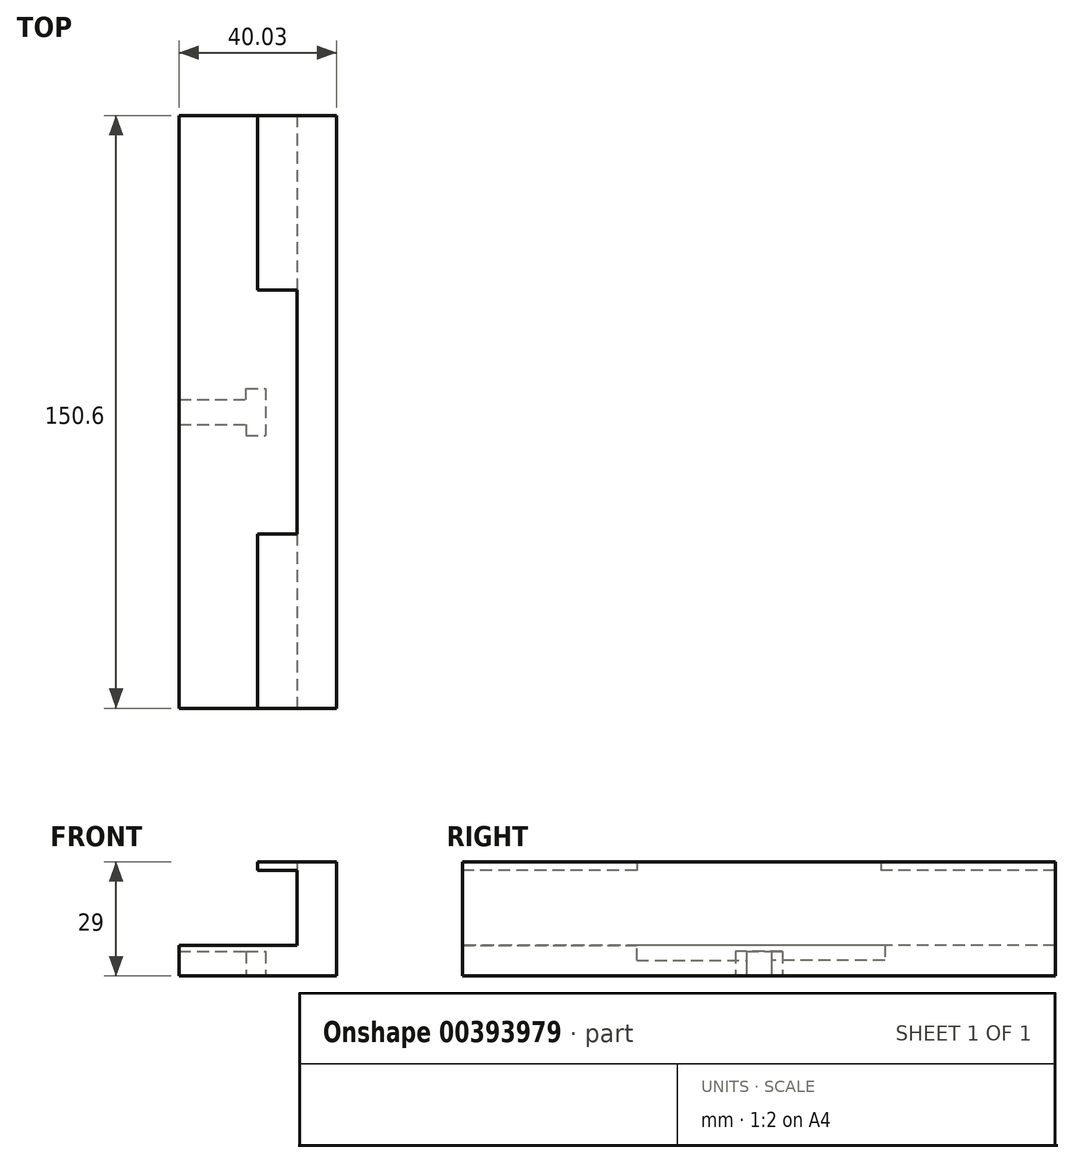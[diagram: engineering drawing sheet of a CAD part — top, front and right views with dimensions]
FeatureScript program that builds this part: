
annotation { "Feature Type Name" : "Feature", "Feature Type Description" : "" }
export const myFeature = defineFeature(function(context is Context, id is Id, definition is map)
    precondition{}
    {
        {
            var Q0;
            Q0=qCreatedBy(makeId("Top.planeOp"),FACE);
            var sketch = newSketch(context, id + "F0", { "sketchPlane" : qUnion([Q0])});
            skLineSegment(sketch, "E0", {"start": v(40.03, 80.64) * mm, "end": v(40.03, -69.96) * mm});
            skLineSegment(sketch, "E1", {"start": v(40.03, 80.64) * mm, "end": v(20.03, 80.64) * mm});
            skLineSegment(sketch, "E2", {"start": v(40.03, -69.96) * mm, "end": v(20.03, -69.96) * mm});
            skLineSegment(sketch, "E3", {"start": v(10.03, -69.96) * mm, "end": v(10.03, -25.66) * mm});
            skLineSegment(sketch, "E4", {"start": v(10.03, 80.64) * mm, "end": v(10.03, 36.34) * mm});
            skLineSegment(sketch, "E5", {"start": v(10.03, -25.66) * mm, "end": v(30.03, -25.66) * mm});
            skLineSegment(sketch, "E6", {"start": v(10.03, 36.34) * mm, "end": v(30.03, 36.34) * mm});
            skLineSegment(sketch, "E7", {"start": v(30.03, -25.66) * mm, "end": v(30.03, 36.34) * mm});
            skLineSegment(sketch, "E8", {"start": v(10.03, 80.64) * mm, "end": v(20.03, 80.64) * mm});
            skLineSegment(sketch, "E9", {"start": v(10.03, -69.96) * mm, "end": v(20.03, -69.96) * mm});
            skSolve(sketch);
        }
        {
            var Q0;
            Q0 = qSketchRegion(id + "F0", true);
            extrude(context, id + "F1", {"entities" : qUnion([Q0]), "depth" : 25 * mm});
        }
        {
            var Q0;
            Q0=makeQuery(id+"F16.boolean.opBoolean","MERGE",FACE,{"derivedFrom":[makeQuery(id+"F14.boolean.opBoolean","MERGE",FACE,{"derivedFrom":[makeQuery(id+"F12.boolean.opBoolean","MERGE",FACE,{"derivedFrom":[makeQuery(id+"F1.opExtrude","CAP_FACE",FACE,{"disambiguationData":[OSD([sQuery(id+"F0.wireOp",EDGE,"E0"),sQuery(id+"F0.wireOp",EDGE,"E1"),sQuery(id+"F0.wireOp",EDGE,"E2"),sQuery(id+"F0.wireOp",EDGE,"E3"),sQuery(id+"F0.wireOp",EDGE,"E4"),sQuery(id+"F0.wireOp",EDGE,"E5"),sQuery(id+"F0.wireOp",EDGE,"E6"),sQuery(id+"F0.wireOp",EDGE,"E7"),sQuery(id+"F0.wireOp",EDGE,"E8"),sQuery(id+"F0.wireOp",EDGE,"E9")])],"isStart":true}),makeQuery(id+"F12.opExtrude","SWEPT_FACE",FACE,{"disambiguationData":[OSD([sQuery(id+"F11.wireOp",EDGE,"E30")])]})]}),makeQuery(id+"F14.opExtrude","SWEPT_FACE",FACE,{"disambiguationData":[OSD([sQuery(id+"F13.wireOp",EDGE,"E34")])]})]}),makeQuery(id+"F16.opExtrude","SWEPT_FACE",FACE,{"disambiguationData":[OSD([sQuery(id+"F15.wireOp",EDGE,"E36")])]})]});
            var sketch = newSketch(context, id + "F2", { "sketchPlane" : qUnion([Q0])});
            skLineSegment(sketch, "E10.bottom", {"start": v(0.03, 69.96) * mm, "end": v(40.03, 69.96) * mm});
            skLineSegment(sketch, "E10.top", {"start": v(0.03, -80.64) * mm, "end": v(40.03, -80.64) * mm});
            skLineSegment(sketch, "E10.left", {"start": v(0.03, 69.96) * mm, "end": v(0.03, -80.64) * mm});
            skLineSegment(sketch, "E10.right", {"start": v(40.03, 69.96) * mm, "end": v(40.03, -80.64) * mm});
            skSolve(sketch);
        }
        {
            var Q0;
            Q0=makeQuery(id+"F1.opExtrude","SWEPT_FACE",FACE,{"disambiguationData":[OSD([sQuery(id+"F0.wireOp",EDGE,"E4")])]});
            var sketch = newSketch(context, id + "F3", { "sketchPlane" : qUnion([Q0])});
            skLineSegment(sketch, "E11", {"start": v(-80.64, 22.8) * mm, "end": v(-36.34, 22.8) * mm});
            skLineSegment(sketch, "E12", {"start": v(-80.64, 22.8) * mm, "end": v(-80.64, 3.8) * mm});
            skLineSegment(sketch, "E13", {"start": v(-80.64, 3.8) * mm, "end": v(-36.34, 3.8) * mm});
            skLineSegment(sketch, "E14", {"start": v(-36.34, 3.8) * mm, "end": v(-36.34, 22.8) * mm});
            skSolve(sketch);
        }
        {
            var Q0;
            Q0 = qSketchRegion(id + "F3", true);
            extrude(context, id + "F4", {"entities" : qUnion([Q0]), "operationType" : NewBodyOperationType.REMOVE, "oppositeDirection" : true, "depth" : 20 * mm});
        }
        {
            var Q0;
            Q0=makeQuery(id+"F1.opExtrude","CAP_FACE",FACE,{"disambiguationData":[OSD([sQuery(id+"F0.wireOp",EDGE,"E0"),sQuery(id+"F0.wireOp",EDGE,"E1"),sQuery(id+"F0.wireOp",EDGE,"E2"),sQuery(id+"F0.wireOp",EDGE,"E3"),sQuery(id+"F0.wireOp",EDGE,"E4"),sQuery(id+"F0.wireOp",EDGE,"E5"),sQuery(id+"F0.wireOp",EDGE,"E6"),sQuery(id+"F0.wireOp",EDGE,"E7"),sQuery(id+"F0.wireOp",EDGE,"E8"),sQuery(id+"F0.wireOp",EDGE,"E9")])],"isStart":false});
            var sketch = newSketch(context, id + "F5", { "sketchPlane" : qUnion([Q0])});
            skLineSegment(sketch, "E15", {"start": v(20.03, 36.34) * mm, "end": v(20.03, 80.64) * mm});
            skLineSegment(sketch, "E16", {"start": v(20.03, 36.34) * mm, "end": v(10.03, 36.34) * mm});
            skLineSegment(sketch, "E17", {"start": v(10.03, 36.34) * mm, "end": v(10.03, 80.64) * mm});
            skLineSegment(sketch, "E18", {"start": v(10.03, 80.64) * mm, "end": v(20.03, 80.64) * mm});
            skSolve(sketch);
        }
        {
            var Q0;
            Q0 = qSketchRegion(id + "F5", true);
            extrude(context, id + "F6", {"entities" : qUnion([Q0]), "operationType" : NewBodyOperationType.REMOVE, "oppositeDirection" : true, "depth" : 25 * mm});
        }
        {
            var Q0;
            Q0=makeQuery(id+"F1.opExtrude","SWEPT_FACE",FACE,{"disambiguationData":[OSD([sQuery(id+"F0.wireOp",EDGE,"E3")])]});
            var sketch = newSketch(context, id + "F7", { "sketchPlane" : qUnion([Q0])});
            skLineSegment(sketch, "E19", {"start": v(25.66, 22.8) * mm, "end": v(69.96, 22.8) * mm});
            skLineSegment(sketch, "E20", {"start": v(25.66, 22.8) * mm, "end": v(25.66, 3.8) * mm});
            skLineSegment(sketch, "E21", {"start": v(69.96, 22.8) * mm, "end": v(69.96, 3.8) * mm});
            skLineSegment(sketch, "E22", {"start": v(25.66, 3.8) * mm, "end": v(69.96, 3.8) * mm});
            skSolve(sketch);
        }
        {
            var Q0;
            Q0 = qSketchRegion(id + "F7", true);
            extrude(context, id + "F8", {"entities" : qUnion([Q0]), "operationType" : NewBodyOperationType.REMOVE, "oppositeDirection" : true, "depth" : 20 * mm});
        }
        {
            var Q0;
            Q0=makeQuery(id+"F1.opExtrude","CAP_FACE",FACE,{"disambiguationData":[OSD([sQuery(id+"F0.wireOp",EDGE,"E0"),sQuery(id+"F0.wireOp",EDGE,"E1"),sQuery(id+"F0.wireOp",EDGE,"E2"),sQuery(id+"F0.wireOp",EDGE,"E3"),sQuery(id+"F0.wireOp",EDGE,"E4"),sQuery(id+"F0.wireOp",EDGE,"E5"),sQuery(id+"F0.wireOp",EDGE,"E6"),sQuery(id+"F0.wireOp",EDGE,"E7"),sQuery(id+"F0.wireOp",EDGE,"E8"),sQuery(id+"F0.wireOp",EDGE,"E9")])],"isStart":false});
            var sketch = newSketch(context, id + "F9", { "sketchPlane" : qUnion([Q0])});
            skLineSegment(sketch, "E23", {"start": v(20.03, -25.66) * mm, "end": v(20.03, -69.96) * mm});
            skLineSegment(sketch, "E24", {"start": v(20.03, -25.66) * mm, "end": v(10.03, -25.66) * mm});
            skLineSegment(sketch, "E25", {"start": v(10.03, -25.66) * mm, "end": v(10.03, -69.96) * mm});
            skLineSegment(sketch, "E26", {"start": v(10.03, -69.96) * mm, "end": v(20.03, -69.96) * mm});
            skSolve(sketch);
        }
        {
            var Q0;
            Q0 = qSketchRegion(id + "F9", true);
            extrude(context, id + "F10", {"entities" : qUnion([Q0]), "operationType" : NewBodyOperationType.REMOVE, "oppositeDirection" : true, "depth" : 25 * mm});
        }
        {
            var Q0;
            Q0=makeQuery(id+"F6.boolean.opBoolean","COPY",FACE,{"disambiguationData":[TD([makeQuery(id+"F4.boolean.opBoolean","COPY",FACE,{"derivedFrom":makeQuery(id+"F4.opExtrude","SWEPT_FACE",FACE,{"disambiguationData":[OSD([sQuery(id+"F3.wireOp",EDGE,"E13")])]})})])],"derivedFrom":makeQuery(id+"F6.opExtrude","SWEPT_FACE",FACE,{"disambiguationData":[OSD([sQuery(id+"F5.wireOp",EDGE,"E15")])]})});
            var sketch = newSketch(context, id + "F11", { "sketchPlane" : qUnion([Q0])});
            skLineSegment(sketch, "E27", {"start": v(-80.64, 0) * mm, "end": v(-80.64, 3.8) * mm});
            skLineSegment(sketch, "E28", {"start": v(-80.64, 3.8) * mm, "end": v(-36.34, 3.8) * mm});
            skLineSegment(sketch, "E29", {"start": v(-36.34, 3.8) * mm, "end": v(-36.34, 0) * mm});
            skLineSegment(sketch, "E30", {"start": v(-36.34, 0) * mm, "end": v(-80.64, 0) * mm});
            skSolve(sketch);
        }
        {
            var Q0;
            Q0 = qSketchRegion(id + "F11", true);
            extrude(context, id + "F12", {"entities" : qUnion([Q0]), "operationType" : NewBodyOperationType.ADD, "depth" : 20 * mm});
        }
        {
            var Q0;
            Q0=makeQuery(id+"F10.boolean.opBoolean","COPY",FACE,{"disambiguationData":[TD([makeQuery(id+"F8.boolean.opBoolean","COPY",FACE,{"derivedFrom":makeQuery(id+"F8.opExtrude","SWEPT_FACE",FACE,{"disambiguationData":[OSD([sQuery(id+"F7.wireOp",EDGE,"E22")])]})})])],"derivedFrom":makeQuery(id+"F10.opExtrude","SWEPT_FACE",FACE,{"disambiguationData":[OSD([sQuery(id+"F9.wireOp",EDGE,"E23")])]})});
            var sketch = newSketch(context, id + "F13", { "sketchPlane" : qUnion([Q0])});
            skLineSegment(sketch, "E31", {"start": v(25.66, 0) * mm, "end": v(25.66, 3.8) * mm});
            skLineSegment(sketch, "E32", {"start": v(25.66, 3.8) * mm, "end": v(69.96, 3.8) * mm});
            skLineSegment(sketch, "E33", {"start": v(69.96, 3.8) * mm, "end": v(69.96, 0) * mm});
            skLineSegment(sketch, "E34", {"start": v(69.96, 0) * mm, "end": v(25.66, 0) * mm});
            skSolve(sketch);
        }
        {
            var Q0;
            Q0 = qSketchRegion(id + "F13", true);
            extrude(context, id + "F14", {"entities" : qUnion([Q0]), "operationType" : NewBodyOperationType.ADD, "depth" : 20 * mm});
        }
        {
            var Q0;
            {var subQ2=sQuery(id+"F7.wireOp",EDGE,"E22");var subQ3=sQuery(id+"F0.wireOp",EDGE,"E5");Q0=makeQuery(id+"F14.boolean.opBoolean","MERGE",FACE,{"derivedFrom":[makeQuery(id+"F8.boolean.opBoolean","SPLIT",FACE,{"disambiguationData":[TD([makeQuery(id+"F8.opExtrude","SWEPT_FACE",FACE,{"disambiguationData":[OSD([subQ2])]})])],"derivedFrom":makeQuery(id+"F1.opExtrude","SWEPT_FACE",FACE,{"disambiguationData":[OSD([subQ3])]})}),makeQuery(id+"F14.opExtrude","SWEPT_FACE",FACE,{"disambiguationData":[OSD([sQuery(id+"F13.wireOp",EDGE,"E31")])]})]});}
            var sketch = newSketch(context, id + "F15", { "sketchPlane" : qUnion([Q0])});
            skLineSegment(sketch, "E35", {"start": v(-30.03, 3.8) * mm, "end": v(-30.03, 0) * mm});
            skLineSegment(sketch, "E36", {"start": v(-30.03, 0) * mm, "end": v(0, 0) * mm});
            skLineSegment(sketch, "E37", {"start": v(0, 0) * mm, "end": v(-0.03, 3.8) * mm});
            skLineSegment(sketch, "E38", {"start": v(-0.03, 3.8) * mm, "end": v(-30.03, 3.8) * mm});
            skSolve(sketch);
        }
        {
            var Q0;
            Q0 = qSketchRegion(id + "F15", true);
            extrude(context, id + "F16", {"entities" : qUnion([Q0]), "operationType" : NewBodyOperationType.ADD, "depth" : 63 * mm});
        }
        {
            var Q0;
            Q0 = qSketchRegion(id + "F2", true);
            extrude(context, id + "F17", {"entities" : qUnion([Q0]), "operationType" : NewBodyOperationType.ADD, "depth" : 4 * mm});
        }
        {
            var Q0;
            Q0=makeQuery(id+"F17.opExtrude","CAP_FACE",FACE,{"disambiguationData":[OSD([sQuery(id+"F2.wireOp",EDGE,"E10.bottom"),sQuery(id+"F2.wireOp",EDGE,"E10.top"),sQuery(id+"F2.wireOp",EDGE,"E10.left"),sQuery(id+"F2.wireOp",EDGE,"E10.right")])],"isStart":false});
            var sketch = newSketch(context, id + "F18", { "sketchPlane" : qUnion([Q0])});
            skLineSegment(sketch, "E39", {"start": v(0.03, -8.5) * mm, "end": v(17.06, -8.5) * mm});
            skLineSegment(sketch, "E40", {"start": v(0.03, -2.2) * mm, "end": v(17.06, -2.2) * mm});
            skLineSegment(sketch, "E41", {"start": v(17.06, -8.5) * mm, "end": v(17.06, -11.34) * mm});
            skLineSegment(sketch, "E42", {"start": v(17.06, -2.2) * mm, "end": v(17.06, 0.66) * mm});
            skLineSegment(sketch, "E43", {"start": v(17.06, -11.34) * mm, "end": v(22.06, -11.34) * mm});
            skLineSegment(sketch, "E44", {"start": v(17.06, 0.66) * mm, "end": v(22.06, 0.66) * mm});
            skLineSegment(sketch, "E45", {"start": v(22.06, -11.34) * mm, "end": v(22.06, 0.66) * mm});
            skLineSegment(sketch, "E46", {"start": v(0.03, -8.5) * mm, "end": v(0.03, -2.2) * mm});
            skSolve(sketch);
        }
        {
            var Q0;
            Q0 = qSketchRegion(id + "F18", true);
            extrude(context, id + "F19", {"entities" : qUnion([Q0]), "operationType" : NewBodyOperationType.REMOVE, "oppositeDirection" : true, "depth" : 6.2 * mm});
        }
        {
            var Q0;
            Q0=makeQuery(id+"F19.boolean.opBoolean","COPY",FACE,{"derivedFrom":makeQuery(id+"F19.opExtrude","SWEPT_FACE",FACE,{"disambiguationData":[OSD([sQuery(id+"F18.wireOp",EDGE,"E46")])]})});
            var sketch = newSketch(context, id + "F20", { "sketchPlane" : qUnion([Q0])});
            skLineSegment(sketch, "E47", {"start": v(8.5, 0) * mm, "end": v(8.5, 2.2) * mm});
            skLineSegment(sketch, "E48", {"start": v(8.5, 2.2) * mm, "end": v(2.2, 2.2) * mm});
            skLineSegment(sketch, "E49", {"start": v(2.2, 2.2) * mm, "end": v(2.2, 0) * mm});
            skLineSegment(sketch, "E50", {"start": v(2.2, 0) * mm, "end": v(8.5, 0) * mm});
            skSolve(sketch);
        }
        {
            var Q0;
            Q0 = qSketchRegion(id + "F20", true);
            extrude(context, id + "F21", {"entities" : qUnion([Q0]), "operationType" : NewBodyOperationType.REMOVE, "oppositeDirection" : true, "depth" : 25 * mm});
        }
    });
